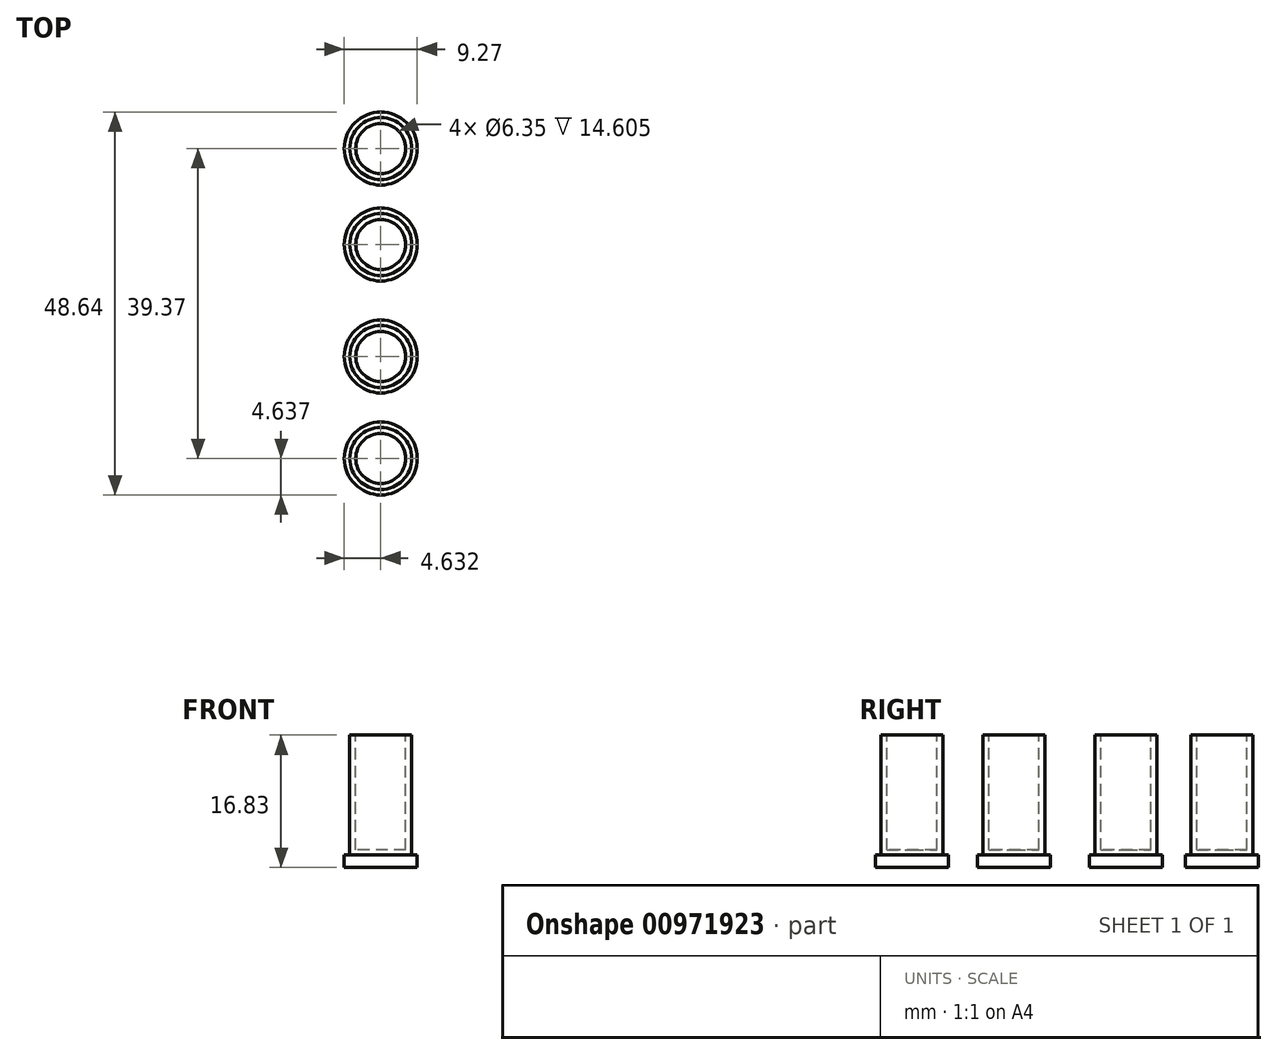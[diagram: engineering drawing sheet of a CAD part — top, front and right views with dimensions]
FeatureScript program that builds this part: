
annotation { "Feature Type Name" : "Feature", "Feature Type Description" : "" }
export const myFeature = defineFeature(function(context is Context, id is Id, definition is map)
    precondition{}
    {
        {
            var Q0;
            Q0=qCreatedBy(makeId("Top.planeOp"),FACE);
            var sketch = newSketch(context, id + "F0", { "sketchPlane" : qUnion([Q0])});
            skLineSegment(sketch, "E0", {"start": v(0, 0) * mm, "end": v(0, 19.81) * mm, "construction": true});
            skLineSegment(sketch, "E1", {"start": v(0, 19.81) * mm, "end": v(22.86, 19.81) * mm, "construction": true});
            skLineSegment(sketch, "E2", {"start": v(22.86, 19.81) * mm, "end": v(22.86, -22.35) * mm, "construction": true});
            skLineSegment(sketch, "E3", {"start": v(22.86, -22.35) * mm, "end": v(0, -22.35) * mm, "construction": true});
            skLineSegment(sketch, "E4", {"start": v(0, -22.35) * mm, "end": v(-22.86, -22.35) * mm, "construction": true});
            skLineSegment(sketch, "E5", {"start": v(-22.86, -22.35) * mm, "end": v(-22.86, 19.52) * mm, "construction": true});
            skLineSegment(sketch, "E6", {"start": v(-22.86, 19.52) * mm, "end": v(0, 19.81) * mm, "construction": true});
            skLineSegment(sketch, "E7", {"start": v(0, 0) * mm, "end": v(0, -22.35) * mm, "construction": true});
            skCircle(sketch, "E8", {"center": v(22.86, 19.81) * mm, "radius": 18.41 * mm});
            skCircle(sketch, "E9", {"center": v(-22.86, 19.52) * mm, "radius": 18.41 * mm});
            skCircle(sketch, "E10", {"center": v(-22.86, -22.35) * mm, "radius": 18.41 * mm});
            skCircle(sketch, "E11", {"center": v(22.86, -22.35) * mm, "radius": 18.41 * mm});
            skCircle(sketch, "E12", {"center": v(-22.86, 19.52) * mm, "radius": 16.51 * mm});
            skCircle(sketch, "E13", {"center": v(22.86, 19.81) * mm, "radius": 16.51 * mm});
            skCircle(sketch, "E14", {"center": v(-22.86, -22.35) * mm, "radius": 16.51 * mm});
            skCircle(sketch, "E15", {"center": v(22.86, -22.35) * mm, "radius": 16.51 * mm});
            skSolve(sketch);
        }
        {
            var Q0;
            Q0=makeQuery(id+"F0.imprint","IMPRINT",FACE,{"disambiguationData":[TD([[makeQuery(id+"F0.imprint","IMPRINT",EDGE,{"derivedFrom":sQuery(id+"F0.wireOp",EDGE,"E9")}),1.0]])]});
            var Q1;
            Q1=makeQuery(id+"F0.imprint","IMPRINT",FACE,{"disambiguationData":[TD([[makeQuery(id+"F0.imprint","IMPRINT",EDGE,{"derivedFrom":sQuery(id+"F0.wireOp",EDGE,"E8")}),1.0]])]});
            var Q2;
            Q2=makeQuery(id+"F0.imprint","IMPRINT",FACE,{"disambiguationData":[TD([[makeQuery(id+"F0.imprint","IMPRINT",EDGE,{"derivedFrom":sQuery(id+"F0.wireOp",EDGE,"E11")}),1.0]])]});
            var Q3;
            Q3=makeQuery(id+"F0.imprint","IMPRINT",FACE,{"disambiguationData":[TD([[makeQuery(id+"F0.imprint","IMPRINT",EDGE,{"derivedFrom":sQuery(id+"F0.wireOp",EDGE,"E10")}),1.0]])]});
            extrude(context, id + "F1", {"entities" : qUnion([Q0, Q1, Q2, Q3]), "depth" : 9.4 * mm, "offsetDistance" : 25.4 * mm});
        }
        {
            var Q0;
            Q0=qCreatedBy(makeId("Top.planeOp"),FACE);
            var sketch = newSketch(context, id + "F2", { "sketchPlane" : qUnion([Q0])});
            skLineSegment(sketch, "E16.bottom", {"start": v(-5.72, 18.03) * mm, "end": v(5.72, 18.03) * mm});
            skLineSegment(sketch, "E16.left", {"start": v(-5.72, 18.03) * mm, "end": v(-5.72, 1.82) * mm});
            skLineSegment(sketch, "E16.right", {"start": v(5.72, 18.03) * mm, "end": v(5.72, 1.82) * mm});
            skLineSegment(sketch, "E17.bottom", {"start": v(-3.64, 16.02) * mm, "end": v(3.7, 16.02) * mm});
            skLineSegment(sketch, "E17.top", {"start": v(-3.64, 6.79) * mm, "end": v(3.7, 6.79) * mm});
            skLineSegment(sketch, "E17.left", {"start": v(-3.64, 16.02) * mm, "end": v(-3.64, 6.79) * mm});
            skLineSegment(sketch, "E17.right", {"start": v(3.7, 16.02) * mm, "end": v(3.7, 6.79) * mm});
            skLineSegment(sketch, "E18.bottom", {"start": v(-3.52, 4.7) * mm, "end": v(3.7, 4.7) * mm});
            skLineSegment(sketch, "E18.top", {"start": v(-3.52, -5.09) * mm, "end": v(3.7, -5.09) * mm});
            skLineSegment(sketch, "E18.left", {"start": v(-3.52, 4.7) * mm, "end": v(-3.52, -5.09) * mm});
            skLineSegment(sketch, "E18.right", {"start": v(3.7, 4.7) * mm, "end": v(3.7, -5.09) * mm});
            skLineSegment(sketch, "E19.bottom", {"start": v(-3.62, -7) * mm, "end": v(3.7, -7) * mm});
            skLineSegment(sketch, "E19.left", {"start": v(-3.62, -7) * mm, "end": v(-3.62, -10.82) * mm});
            skLineSegment(sketch, "E19.right", {"start": v(3.7, -7) * mm, "end": v(3.7, -10.82) * mm});
            skLineSegment(sketch, "E20.bottom", {"start": v(-5.72, 1.82) * mm, "end": v(-8.73, 1.82) * mm});
            skLineSegment(sketch, "E20.top", {"start": v(-5.72, -1.69) * mm, "end": v(-8.73, -1.69) * mm});
            skPoint(sketch, "E21.oppositeSnap0", {"position": v(-8.73, 0.07) * mm});
            skLineSegment(sketch, "E21.bottom", {"start": v(-10.64, 3.2) * mm, "end": v(-8.73, 3.2) * mm});
            skLineSegment(sketch, "E21.top", {"start": v(-10.64, -3.6) * mm, "end": v(-8.73, -3.6) * mm});
            skLineSegment(sketch, "E21.left", {"start": v(-10.64, 3.2) * mm, "end": v(-10.64, -3.6) * mm});
            skLineSegment(sketch, "E21.right", {"start": v(-8.73, 3.2) * mm, "end": v(-8.73, 1.82) * mm});
            skLineSegment(sketch, "E22.trimOffspring", {"start": v(-8.73, -1.69) * mm, "end": v(-8.73, -3.6) * mm});
            skLineSegment(sketch, "E23.MirrorCS", {"start": v(10.64, 3.2) * mm, "end": v(10.64, -3.6) * mm});
            skLineSegment(sketch, "E24.MirrorCS", {"start": v(10.64, 3.2) * mm, "end": v(8.73, 3.2) * mm});
            skLineSegment(sketch, "E25.MirrorCS", {"start": v(8.73, 3.2) * mm, "end": v(8.73, 1.82) * mm});
            skLineSegment(sketch, "E26.MirrorCS", {"start": v(5.72, 1.82) * mm, "end": v(8.73, 1.82) * mm});
            skLineSegment(sketch, "E27.MirrorCS", {"start": v(5.72, -1.69) * mm, "end": v(8.73, -1.69) * mm});
            skLineSegment(sketch, "E28.MirrorCS", {"start": v(8.73, -1.69) * mm, "end": v(8.73, -3.6) * mm});
            skLineSegment(sketch, "E29.MirrorCS", {"start": v(10.64, -3.6) * mm, "end": v(8.73, -3.6) * mm});
            skLineSegment(sketch, "E30.trimOffspring", {"start": v(-5.72, -1.69) * mm, "end": v(-5.72, -10.82) * mm});
            skLineSegment(sketch, "E31.trimOffspring", {"start": v(5.72, -1.69) * mm, "end": v(5.72, -10.82) * mm});
            skLineSegment(sketch, "E32", {"start": v(-8.63, -10.82) * mm, "end": v(-5.72, -10.82) * mm});
            skPoint(sketch, "E33.orphan", {"position": v(3.7, -15.62) * mm});
            skLineSegment(sketch, "E34", {"start": v(-7.93, -12.78) * mm, "end": v(8.89, -12.78) * mm});
            skLineSegment(sketch, "E35", {"start": v(8.89, -12.78) * mm, "end": v(9.58, -10.82) * mm});
            skLineSegment(sketch, "E36", {"start": v(-8.63, -10.82) * mm, "end": v(-7.93, -12.78) * mm});
            skLineSegment(sketch, "E37.trimOffspring", {"start": v(-3.62, -10.82) * mm, "end": v(3.7, -10.82) * mm});
            skLineSegment(sketch, "E38.trimOffspring", {"start": v(5.72, -10.82) * mm, "end": v(9.58, -10.82) * mm});
            skSolve(sketch);
        }
        {
            var Q0;
            Q0=makeQuery(id+"F2.imprint","IMPRINT",FACE,{"disambiguationData":[TD([[makeQuery(id+"F2.imprint","IMPRINT",EDGE,{"derivedFrom":sQuery(id+"F2.wireOp",EDGE,"E16.bottom")}),-1.0]])]});
            extrude(context, id + "F3", {"entities" : qUnion([Q0]), "depth" : 1.27 * mm, "offsetDistance" : 25.4 * mm});
        }
        {
            var Q0;
            Q0=qCreatedBy(makeId("Top.planeOp"),FACE);
            var sketch = newSketch(context, id + "F4", { "sketchPlane" : qUnion([Q0])});
            skCircle(sketch, "E39", {"center": v(-22.86, 19.52) * mm, "radius": 4.06 * mm});
            skCircle(sketch, "E40", {"center": v(22.86, 19.81) * mm, "radius": 4.06 * mm});
            skCircle(sketch, "E41", {"center": v(22.86, -22.35) * mm, "radius": 4.06 * mm});
            skCircle(sketch, "E42", {"center": v(-22.86, -22.35) * mm, "radius": 4.06 * mm});
            skCircle(sketch, "E43", {"center": v(-22.86, 19.52) * mm, "radius": 2.8 * mm});
            skCircle(sketch, "E44", {"center": v(22.86, 19.81) * mm, "radius": 2.8 * mm});
            skCircle(sketch, "E45", {"center": v(-22.86, -22.35) * mm, "radius": 2.8 * mm});
            skCircle(sketch, "E46", {"center": v(22.86, -22.35) * mm, "radius": 2.8 * mm});
            skSolve(sketch);
        }
        {
            var Q0;
            Q0=makeQuery(id+"F4.imprint","IMPRINT",FACE,{"disambiguationData":[TD([[makeQuery(id+"F4.imprint","IMPRINT",EDGE,{"derivedFrom":sQuery(id+"F4.wireOp",EDGE,"E40")}),1.0]])]});
            var Q1;
            Q1=makeQuery(id+"F4.imprint","IMPRINT",FACE,{"disambiguationData":[TD([[makeQuery(id+"F4.imprint","IMPRINT",EDGE,{"derivedFrom":sQuery(id+"F4.wireOp",EDGE,"E39")}),1.0]])]});
            var Q2;
            Q2=makeQuery(id+"F4.imprint","IMPRINT",FACE,{"disambiguationData":[TD([[makeQuery(id+"F4.imprint","IMPRINT",EDGE,{"derivedFrom":sQuery(id+"F4.wireOp",EDGE,"E42")}),1.0]])]});
            var Q3;
            Q3=makeQuery(id+"F4.imprint","IMPRINT",FACE,{"disambiguationData":[TD([[makeQuery(id+"F4.imprint","IMPRINT",EDGE,{"derivedFrom":sQuery(id+"F4.wireOp",EDGE,"E41")}),1.0]])]});
            extrude(context, id + "F5", {"entities" : qUnion([Q0, Q1, Q2, Q3]), "depth" : 5.08 * mm, "offsetDistance" : 25.4 * mm});
        }
        {
            var Q0;
            Q0=qCreatedBy(makeId("Top.planeOp"),FACE);
            var sketch = newSketch(context, id + "F6", { "sketchPlane" : qUnion([Q0])});
            skLineSegment(sketch, "E47", {"start": v(-21.68, 16.38) * mm, "end": v(-15.36, 3.99) * mm});
            skLineSegment(sketch, "E48", {"start": v(-15.36, 3.99) * mm, "end": v(-14.18, 4.59) * mm});
            skLineSegment(sketch, "E49", {"start": v(-14.18, 4.59) * mm, "end": v(-20.46, 16.89) * mm});
            skLineSegment(sketch, "E50", {"start": v(-20.46, 16.89) * mm, "end": v(-21.68, 16.38) * mm});
            skLineSegment(sketch, "E51.1.0", {"start": v(-21.75, 22.98) * mm, "end": v(-20.7, 22.17) * mm});
            skLineSegment(sketch, "E51.1.1", {"start": v(-20.7, 22.17) * mm, "end": v(-13.13, 33.84) * mm});
            skLineSegment(sketch, "E51.1.2", {"start": v(-14.23, 34.56) * mm, "end": v(-21.75, 22.98) * mm});
            skLineSegment(sketch, "E51.1.3", {"start": v(-13.13, 33.84) * mm, "end": v(-14.23, 34.56) * mm});
            skLineSegment(sketch, "E51.2.0", {"start": v(-26.38, 18.81) * mm, "end": v(-26.2, 20.13) * mm});
            skLineSegment(sketch, "E51.2.1", {"start": v(-26.2, 20.13) * mm, "end": v(-40.1, 20.85) * mm});
            skLineSegment(sketch, "E51.2.2", {"start": v(-40.16, 19.53) * mm, "end": v(-26.38, 18.81) * mm});
            skLineSegment(sketch, "E51.2.3", {"start": v(-40.1, 20.85) * mm, "end": v(-40.16, 19.53) * mm});
            skPoint(sketch, "E51.center", {"position": v(-22.86, 19.56) * mm});
            skLineSegment(sketch, "E52.MirrorCS", {"start": v(20.46, 16.89) * mm, "end": v(21.68, 16.38) * mm});
            skLineSegment(sketch, "E53.MirrorCS", {"start": v(21.68, 16.38) * mm, "end": v(15.36, 3.99) * mm});
            skLineSegment(sketch, "E54.MirrorCS", {"start": v(14.18, 4.59) * mm, "end": v(20.46, 16.89) * mm});
            skLineSegment(sketch, "E55.MirrorCS", {"start": v(15.36, 3.99) * mm, "end": v(14.18, 4.59) * mm});
            skLineSegment(sketch, "E56.1.0", {"start": v(26.47, 19.06) * mm, "end": v(26.3, 20.38) * mm});
            skLineSegment(sketch, "E56.1.1", {"start": v(40.26, 19.78) * mm, "end": v(26.47, 19.06) * mm});
            skLineSegment(sketch, "E56.1.2", {"start": v(26.3, 20.38) * mm, "end": v(40.19, 21.1) * mm});
            skLineSegment(sketch, "E56.1.3", {"start": v(40.19, 21.1) * mm, "end": v(40.26, 19.78) * mm});
            skLineSegment(sketch, "E56.2.0", {"start": v(21.58, 23.18) * mm, "end": v(20.53, 22.37) * mm});
            skLineSegment(sketch, "E56.2.1", {"start": v(14.06, 34.76) * mm, "end": v(21.58, 23.18) * mm});
            skLineSegment(sketch, "E56.2.2", {"start": v(20.53, 22.37) * mm, "end": v(12.96, 34.05) * mm});
            skLineSegment(sketch, "E56.2.3", {"start": v(12.96, 34.05) * mm, "end": v(14.06, 34.76) * mm});
            skPoint(sketch, "E56.center", {"position": v(22.83, 19.71) * mm});
            skLineSegment(sketch, "E57.MirrorCS", {"start": v(15.36, -6.83) * mm, "end": v(14.18, -7.44) * mm});
            skLineSegment(sketch, "E58.MirrorCS", {"start": v(14.18, -7.44) * mm, "end": v(20.46, -19.73) * mm});
            skLineSegment(sketch, "E59.MirrorCS", {"start": v(21.68, -19.23) * mm, "end": v(15.36, -6.83) * mm});
            skLineSegment(sketch, "E60.MirrorCS", {"start": v(20.46, -19.73) * mm, "end": v(21.68, -19.23) * mm});
            skLineSegment(sketch, "E61.MirrorCS", {"start": v(26.47, -21.91) * mm, "end": v(26.3, -23.23) * mm});
            skLineSegment(sketch, "E62.MirrorCS", {"start": v(40.26, -22.63) * mm, "end": v(26.47, -21.91) * mm});
            skLineSegment(sketch, "E63.MirrorCS", {"start": v(26.3, -23.23) * mm, "end": v(40.19, -23.95) * mm});
            skLineSegment(sketch, "E64.MirrorCS", {"start": v(40.19, -23.95) * mm, "end": v(40.26, -22.63) * mm});
            skLineSegment(sketch, "E65.MirrorCS", {"start": v(21.58, -26.03) * mm, "end": v(20.53, -25.22) * mm});
            skLineSegment(sketch, "E66.MirrorCS", {"start": v(20.53, -25.22) * mm, "end": v(12.96, -36.9) * mm});
            skLineSegment(sketch, "E67.MirrorCS", {"start": v(14.06, -37.61) * mm, "end": v(21.58, -26.03) * mm});
            skLineSegment(sketch, "E68.MirrorCS", {"start": v(12.96, -36.9) * mm, "end": v(14.06, -37.61) * mm});
            skLineSegment(sketch, "E69.MirrorCS", {"start": v(-15.36, -6.83) * mm, "end": v(-14.18, -7.44) * mm});
            skLineSegment(sketch, "E70.MirrorCS", {"start": v(-21.68, -19.23) * mm, "end": v(-15.36, -6.83) * mm});
            skLineSegment(sketch, "E71.MirrorCS", {"start": v(-14.18, -7.44) * mm, "end": v(-20.46, -19.73) * mm});
            skLineSegment(sketch, "E72.MirrorCS", {"start": v(-20.46, -19.73) * mm, "end": v(-21.68, -19.23) * mm});
            skLineSegment(sketch, "E73.MirrorCS", {"start": v(-26.38, -21.66) * mm, "end": v(-26.2, -22.98) * mm});
            skLineSegment(sketch, "E74.MirrorCS", {"start": v(-40.16, -22.38) * mm, "end": v(-26.38, -21.66) * mm});
            skLineSegment(sketch, "E75.MirrorCS", {"start": v(-26.2, -22.98) * mm, "end": v(-40.1, -23.7) * mm});
            skLineSegment(sketch, "E76.MirrorCS", {"start": v(-40.1, -23.7) * mm, "end": v(-40.16, -22.38) * mm});
            skLineSegment(sketch, "E77.MirrorCS", {"start": v(-21.75, -25.82) * mm, "end": v(-20.7, -25.01) * mm});
            skLineSegment(sketch, "E78.MirrorCS", {"start": v(-14.23, -37.4) * mm, "end": v(-21.75, -25.82) * mm});
            skLineSegment(sketch, "E79.MirrorCS", {"start": v(-20.7, -25.01) * mm, "end": v(-13.13, -36.69) * mm});
            skLineSegment(sketch, "E80.MirrorCS", {"start": v(-13.13, -36.69) * mm, "end": v(-14.23, -37.4) * mm});
            skSolve(sketch);
        }
        {
            var Q0;
            Q0=makeQuery(id+"F6.imprint","IMPRINT",FACE,{"disambiguationData":[TD([[makeQuery(id+"F6.imprint","IMPRINT",EDGE,{"derivedFrom":sQuery(id+"F6.wireOp",EDGE,"E51.1.0")}),1.0]])]});
            var Q1;
            Q1=makeQuery(id+"F6.imprint","IMPRINT",FACE,{"disambiguationData":[TD([[makeQuery(id+"F6.imprint","IMPRINT",EDGE,{"derivedFrom":sQuery(id+"F6.wireOp",EDGE,"E51.2.0")}),1.0]])]});
            var Q2;
            Q2=makeQuery(id+"F6.imprint","IMPRINT",FACE,{"disambiguationData":[TD([[makeQuery(id+"F6.imprint","IMPRINT",EDGE,{"derivedFrom":sQuery(id+"F6.wireOp",EDGE,"E47")}),1.0]])]});
            var Q3;
            Q3=makeQuery(id+"F6.imprint","IMPRINT",FACE,{"disambiguationData":[TD([[makeQuery(id+"F6.imprint","IMPRINT",EDGE,{"derivedFrom":sQuery(id+"F6.wireOp",EDGE,"E69.MirrorCS")}),-1.0]])]});
            var Q4;
            Q4=makeQuery(id+"F6.imprint","IMPRINT",FACE,{"disambiguationData":[TD([[makeQuery(id+"F6.imprint","IMPRINT",EDGE,{"derivedFrom":sQuery(id+"F6.wireOp",EDGE,"E73.MirrorCS")}),-1.0]])]});
            var Q5;
            Q5=makeQuery(id+"F6.imprint","IMPRINT",FACE,{"disambiguationData":[TD([[makeQuery(id+"F6.imprint","IMPRINT",EDGE,{"derivedFrom":sQuery(id+"F6.wireOp",EDGE,"E77.MirrorCS")}),-1.0]])]});
            var Q6;
            Q6=makeQuery(id+"F6.imprint","IMPRINT",FACE,{"disambiguationData":[TD([[makeQuery(id+"F6.imprint","IMPRINT",EDGE,{"derivedFrom":sQuery(id+"F6.wireOp",EDGE,"E57.MirrorCS")}),1.0]])]});
            var Q7;
            Q7=makeQuery(id+"F6.imprint","IMPRINT",FACE,{"disambiguationData":[TD([[makeQuery(id+"F6.imprint","IMPRINT",EDGE,{"derivedFrom":sQuery(id+"F6.wireOp",EDGE,"E65.MirrorCS")}),1.0]])]});
            var Q8;
            Q8=makeQuery(id+"F6.imprint","IMPRINT",FACE,{"disambiguationData":[TD([[makeQuery(id+"F6.imprint","IMPRINT",EDGE,{"derivedFrom":sQuery(id+"F6.wireOp",EDGE,"E61.MirrorCS")}),1.0]])]});
            var Q9;
            Q9=makeQuery(id+"F6.imprint","IMPRINT",FACE,{"disambiguationData":[TD([[makeQuery(id+"F6.imprint","IMPRINT",EDGE,{"derivedFrom":sQuery(id+"F6.wireOp",EDGE,"E52.MirrorCS")}),-1.0]])]});
            var Q10;
            Q10=makeQuery(id+"F6.imprint","IMPRINT",FACE,{"disambiguationData":[TD([[makeQuery(id+"F6.imprint","IMPRINT",EDGE,{"derivedFrom":sQuery(id+"F6.wireOp",EDGE,"E56.1.0")}),-1.0]])]});
            var Q11;
            Q11=makeQuery(id+"F6.imprint","IMPRINT",FACE,{"disambiguationData":[TD([[makeQuery(id+"F6.imprint","IMPRINT",EDGE,{"derivedFrom":sQuery(id+"F6.wireOp",EDGE,"E56.2.0")}),-1.0]])]});
            extrude(context, id + "F7", {"entities" : qUnion([Q0, Q1, Q2, Q3, Q4, Q5, Q6, Q7, Q8, Q9, Q10, Q11]), "operationType" : NewBodyOperationType.ADD, "depth" : 3.8 * mm, "offsetDistance" : 25.4 * mm});
        }
        {
            var Q0;
            Q0=qCreatedBy(makeId("Top.planeOp"),FACE);
            var sketch = newSketch(context, id + "F8", { "sketchPlane" : qUnion([Q0])});
            skLineSegment(sketch, "E81", {"start": v(-22.86, 19.52) * mm, "end": v(-22.86, -65.3) * mm, "construction": true});
            skLineSegment(sketch, "E82", {"start": v(22.59, 19.82) * mm, "end": v(22.59, -63.66) * mm, "construction": true});
            skLineSegment(sketch, "E83", {"start": v(-22.86, -22.35) * mm, "end": v(49.1, -22.35) * mm, "construction": true});
            skLineSegment(sketch, "E84", {"start": v(-22.86, 19.52) * mm, "end": v(46.6, 19.52) * mm, "construction": true});
            skLineSegment(sketch, "E85.bottom", {"start": v(-22.86, 2.2) * mm, "end": v(-21.59, 2.2) * mm});
            skLineSegment(sketch, "E85.top", {"start": v(-22.86, -4.69) * mm, "end": v(-21.59, -4.69) * mm});
            skLineSegment(sketch, "E85.left", {"start": v(-22.86, 2.2) * mm, "end": v(-22.86, -4.69) * mm});
            skLineSegment(sketch, "E85.right", {"start": v(-21.59, 2.2) * mm, "end": v(-21.59, -4.69) * mm});
            skLineSegment(sketch, "E86.bottom", {"start": v(22.59, 2.68) * mm, "end": v(21.32, 2.68) * mm});
            skLineSegment(sketch, "E86.top", {"start": v(22.59, -5.17) * mm, "end": v(21.32, -5.17) * mm});
            skLineSegment(sketch, "E86.left", {"start": v(22.59, 2.68) * mm, "end": v(22.59, -5.17) * mm});
            skLineSegment(sketch, "E86.right", {"start": v(21.32, 2.68) * mm, "end": v(21.32, -5.17) * mm});
            skLineSegment(sketch, "E87.bottom", {"start": v(-5.05, 18.04) * mm, "end": v(5.32, 18.04) * mm});
            skLineSegment(sketch, "E87.top", {"start": v(-5.05, 16.77) * mm, "end": v(5.32, 16.77) * mm});
            skLineSegment(sketch, "E87.left", {"start": v(-5.05, 18.04) * mm, "end": v(-5.05, 16.77) * mm});
            skLineSegment(sketch, "E87.right", {"start": v(5.32, 18.04) * mm, "end": v(5.32, 16.77) * mm});
            skLineSegment(sketch, "E88", {"start": v(0, 16.77) * mm, "end": v(0, -13.2) * mm, "construction": true});
            skLineSegment(sketch, "E89", {"start": v(0, -13.2) * mm, "end": v(8.5, -13.2) * mm});
            skLineSegment(sketch, "E90", {"start": v(8.5, -13.2) * mm, "end": v(10, -11.45) * mm});
            skLineSegment(sketch, "E91", {"start": v(10, -11.45) * mm, "end": v(-9.63, -11.45) * mm});
            skLineSegment(sketch, "E92", {"start": v(-9.63, -11.45) * mm, "end": v(-8.14, -13.2) * mm});
            skLineSegment(sketch, "E93", {"start": v(-8.14, -13.2) * mm, "end": v(0, -13.2) * mm});
            skSolve(sketch);
        }
        {
            var Q0;
            Q0=makeQuery(id+"F8.imprint","IMPRINT",FACE,{"disambiguationData":[TD([[makeQuery(id+"F8.imprint","IMPRINT",EDGE,{"derivedFrom":sQuery(id+"F8.wireOp",EDGE,"E85.bottom")}),-1.0]])]});
            var Q1;
            Q1=makeQuery(id+"F8.imprint","IMPRINT",FACE,{"disambiguationData":[TD([[makeQuery(id+"F8.imprint","IMPRINT",EDGE,{"derivedFrom":sQuery(id+"F8.wireOp",EDGE,"E87.bottom")}),-1.0]])]});
            var Q2;
            Q2=makeQuery(id+"F8.imprint","IMPRINT",FACE,{"disambiguationData":[TD([[makeQuery(id+"F8.imprint","IMPRINT",EDGE,{"derivedFrom":sQuery(id+"F8.wireOp",EDGE,"9rF1tbs7-q54x-uDNo-DJnV-IEAHex31H44c.bottom")}),1.0]])]});
            var Q3;
            Q3=makeQuery(id+"F8.imprint","IMPRINT",FACE,{"disambiguationData":[TD([[makeQuery(id+"F8.imprint","IMPRINT",EDGE,{"derivedFrom":sQuery(id+"F8.wireOp",EDGE,"E86.bottom")}),1.0]])]});
            var Q4;
            Q4=makeQuery(id+"F8.imprint","IMPRINT",FACE,{"disambiguationData":[TD([[makeQuery(id+"F8.imprint","IMPRINT",EDGE,{"derivedFrom":sQuery(id+"F8.wireOp",EDGE,"E89")}),1.0]])]});
            extrude(context, id + "F9", {"entities" : qUnion([Q0, Q1, Q2, Q3, Q4]), "operationType" : NewBodyOperationType.ADD, "depth" : 5.6 * mm, "offsetDistance" : 25.4 * mm});
        }
        {
            var Q0;
            Q0=qCreatedBy(makeId("Top.planeOp"),FACE);
            var sketch = newSketch(context, id + "F10", { "sketchPlane" : qUnion([Q0])});
            skCircle(sketch, "E94", {"center": v(0, 17.78) * mm, "radius": 1.78 * mm});
            skCircle(sketch, "E95.MirrorC", {"center": v(0, -12.17) * mm, "radius": 1.78 * mm});
            skCircle(sketch, "E96", {"center": v(-22.35, -0.97) * mm, "radius": 1.65 * mm});
            skCircle(sketch, "E97.MirrorC", {"center": v(22.2, -0.97) * mm, "radius": 1.65 * mm});
            skSolve(sketch);
        }
        {
            var Q0;
            Q0=makeQuery(id+"F10.imprint","IMPRINT",FACE,{"disambiguationData":[TD([[makeQuery(id+"F10.imprint","IMPRINT",EDGE,{"derivedFrom":sQuery(id+"F10.wireOp",EDGE,"E96")}),1.0]])]});
            var Q1;
            Q1=makeQuery(id+"F10.imprint","IMPRINT",FACE,{"disambiguationData":[TD([[makeQuery(id+"F10.imprint","IMPRINT",EDGE,{"derivedFrom":sQuery(id+"F10.wireOp",EDGE,"E95.MirrorC")}),-1.0]])]});
            var Q2;
            Q2=makeQuery(id+"F10.imprint","IMPRINT",FACE,{"disambiguationData":[TD([[makeQuery(id+"F10.imprint","IMPRINT",EDGE,{"derivedFrom":sQuery(id+"F10.wireOp",EDGE,"E97.MirrorC")}),-1.0]])]});
            var Q3;
            Q3=makeQuery(id+"F10.imprint","IMPRINT",FACE,{"disambiguationData":[TD([[makeQuery(id+"F10.imprint","IMPRINT",EDGE,{"derivedFrom":sQuery(id+"F10.wireOp",EDGE,"E94")}),1.0]])]});
            extrude(context, id + "F11", {"entities" : qUnion([Q0, Q1, Q2, Q3]), "operationType" : NewBodyOperationType.ADD, "depth" : 7.62 * mm, "offsetDistance" : 25.4 * mm});
        }
        {
            var Q0;
            Q0=sQuery(id+"F10.wireOp",VERTEX,"E94.center");
            var Q1;
            Q1=sQuery(id+"F10.wireOp",VERTEX,"E96.center");
            var Q2;
            Q2=sQuery(id+"F10.wireOp",VERTEX,"E95.MirrorC.center");
            var Q3;
            Q3=sQuery(id+"F10.wireOp",VERTEX,"E97.MirrorC.center");
            var Q4;
            Q4=makeQuery(id+"F1.opExtrude","SWEPT_BODY",BODY,{"disambiguationData":[OSD([sQuery(id+"F0.wireOp",EDGE,"E8"),sQuery(id+"F0.wireOp",EDGE,"E13")])]});
            hole(context, id + "F12", {"style" : HoleStyle.SIMPLE, "endStyle" : HoleEndStyle.THROUGH, "oppositeDirection" : true, "holeDiameter" : 0.76 * mm, "majorDiameter" : 6.35 * mm, "isTappedThrough" : true, "tappedDepth" : 12.7 * mm, "tapClearance" : 3, "locations" : qUnion([Q0, Q1, Q2, Q3]), "scope" : qUnion([Q4])});
        }
        {
            var Q0;
            Q0=makeQuery(id+"F1.opExtrude","CAP_EDGE",EDGE,{"disambiguationData":[OSD([sQuery(id+"F0.wireOp",EDGE,"E12")])],"isStart":false});
            var Q1;
            Q1=makeQuery(id+"F1.opExtrude","CAP_EDGE",EDGE,{"disambiguationData":[OSD([sQuery(id+"F0.wireOp",EDGE,"E14")])],"isStart":false});
            var Q2;
            Q2=makeQuery(id+"F1.opExtrude","CAP_EDGE",EDGE,{"disambiguationData":[OSD([sQuery(id+"F0.wireOp",EDGE,"E15")])],"isStart":false});
            var Q3;
            Q3=makeQuery(id+"F1.opExtrude","CAP_EDGE",EDGE,{"disambiguationData":[OSD([sQuery(id+"F0.wireOp",EDGE,"E13")])],"isStart":false});
            chamfer(context, id + "F13", {"entities" : qUnion([Q0, Q1, Q2, Q3]), "width" : 2.54 * mm, "tangentPropagation" : true});
        }
        {
            var Q0;
            Q0=qCreatedBy(makeId("Top.planeOp"),FACE);
            var sketch = newSketch(context, id + "F14", { "sketchPlane" : qUnion([Q0])});
            skCircle(sketch, "E98", {"center": v(46.75, 22.29) * mm, "radius": 4.64 * mm});
            skSolve(sketch);
        }
        {
            var Q0;
            Q0=makeQuery(id+"F14.imprint","IMPRINT",FACE,{"disambiguationData":[TD([[makeQuery(id+"F14.imprint","IMPRINT",EDGE,{"derivedFrom":sQuery(id+"F14.wireOp",EDGE,"E98")}),1.0]])]});
            extrude(context, id + "F15", {"entities" : qUnion([Q0]), "depth" : 1.59 * mm, "offsetDistance" : 25.4 * mm});
        }
        {
            var Q0;
            Q0=makeQuery(id+"F15.opExtrude","CAP_FACE",FACE,{"disambiguationData":[OSD([sQuery(id+"F14.wireOp",EDGE,"E98")])],"isStart":false});
            var sketch = newSketch(context, id + "F16", { "sketchPlane" : qUnion([Q0])});
            skCircle(sketch, "E99", {"center": v(46.75, 22.29) * mm, "radius": 3.94 * mm});
            skSolve(sketch);
        }
        {
            var Q0;
            Q0=makeQuery(id+"F16.imprint","IMPRINT",FACE,{"disambiguationData":[TD([[makeQuery(id+"F16.imprint","IMPRINT",EDGE,{"derivedFrom":sQuery(id+"F16.wireOp",EDGE,"E99")}),1.0]])]});
            extrude(context, id + "F17", {"entities" : qUnion([Q0]), "operationType" : NewBodyOperationType.ADD, "depth" : 15.24 * mm, "offsetDistance" : 25.4 * mm});
        }
        {
            var Q0;
            Q0=makeQuery(id+"F17.opExtrude","CAP_FACE",FACE,{"disambiguationData":[OSD([sQuery(id+"F16.wireOp",EDGE,"E99")])],"isStart":false});
            var sketch = newSketch(context, id + "F18", { "sketchPlane" : qUnion([Q0])});
            skCircle(sketch, "E100", {"center": v(46.75, 22.29) * mm, "radius": 3.18 * mm});
            skSolve(sketch);
        }
        {
            var Q0;
            Q0=makeQuery(id+"F18.imprint","IMPRINT",FACE,{"disambiguationData":[TD([[makeQuery(id+"F18.imprint","IMPRINT",EDGE,{"derivedFrom":sQuery(id+"F18.wireOp",EDGE,"E100")}),1.0]])]});
            extrude(context, id + "F19", {"entities" : qUnion([Q0]), "operationType" : NewBodyOperationType.REMOVE, "oppositeDirection" : true, "depth" : 14.6 * mm, "offsetDistance" : 25.4 * mm});
        }
        {
            var Q0;
            Q0=makeQuery(id+"F15.opExtrude","SWEPT_BODY",BODY,{"disambiguationData":[OSD([sQuery(id+"F14.wireOp",EDGE,"E98")])]});
            transform(context, id + "F20", {"entities" : qUnion([Q0]), "transformType" : TransformType.TRANSLATION_3D, "dx" : 0 * mm, "dy" : -12.2 * mm, "dz" : 0 * mm, "makeCopy" : true});
        }
        {
            var Q0;
            Q0=makeQuery(id+"F15.opExtrude","SWEPT_BODY",BODY,{"disambiguationData":[OSD([sQuery(id+"F14.wireOp",EDGE,"E98")])]});
            transform(context, id + "F21", {"entities" : qUnion([Q0]), "transformType" : TransformType.TRANSLATION_3D, "dx" : 0 * mm, "dy" : -26.42 * mm, "dz" : 0 * mm, "makeCopy" : true});
        }
        {
            var Q0;
            Q0=makeQuery(id+"F15.opExtrude","SWEPT_BODY",BODY,{"disambiguationData":[OSD([sQuery(id+"F14.wireOp",EDGE,"E98")])]});
            transform(context, id + "F22", {"entities" : qUnion([Q0]), "transformType" : TransformType.TRANSLATION_3D, "dx" : 0 * mm, "dy" : -39.37 * mm, "dz" : 0 * mm, "makeCopy" : true});
        }
    });
